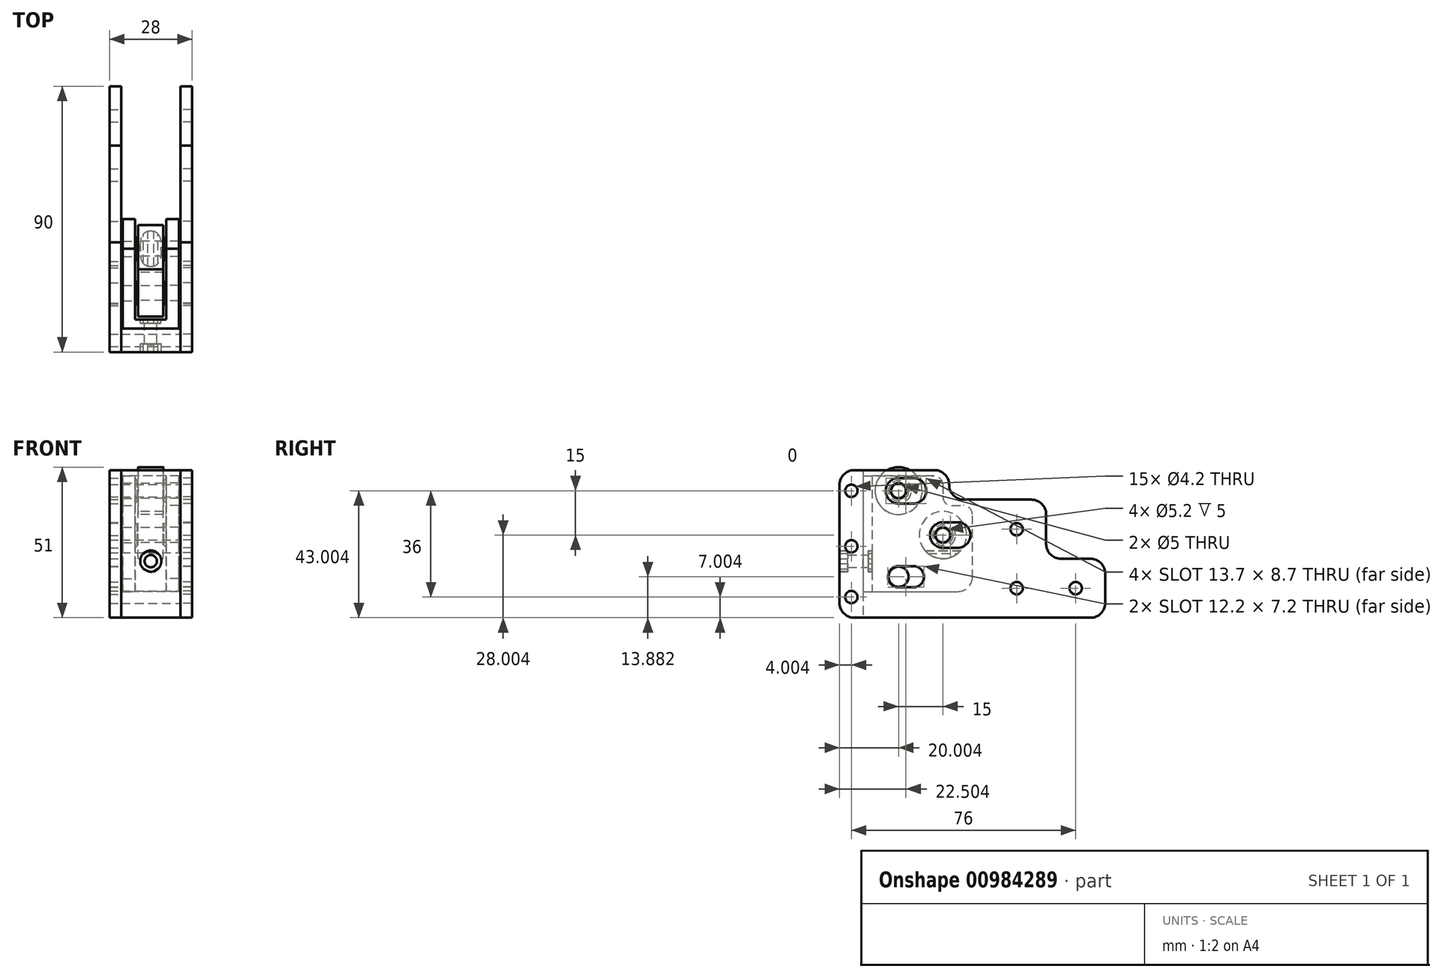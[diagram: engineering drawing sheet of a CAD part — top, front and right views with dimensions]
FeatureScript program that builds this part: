
annotation { "Feature Type Name" : "Feature", "Feature Type Description" : "" }
export const myFeature = defineFeature(function(context is Context, id is Id, definition is map)
    precondition{}
    {
        {
            var Q0;
            Q0=qCreatedBy(makeId("Right.planeOp"),FACE);
            var sketch = newSketch(context, id + "F0", { "sketchPlane" : qUnion([Q0])});
            skLineSegment(sketch, "E0.top", {"start": v(-51.77, -24.19) * mm, "end": v(28.23, -24.19) * mm});
            skLineSegment(sketch, "E0.left", {"start": v(-56.77, 20.81) * mm, "end": v(-56.77, -19.19) * mm});
            skCircle(sketch, "E1", {"center": v(23.23, -14.19) * mm, "radius": 2.1 * mm});
            skCircle(sketch, "E2", {"center": v(3.23, -14.19) * mm, "radius": 2.1 * mm});
            skCircle(sketch, "E3", {"center": v(3.23, 5.81) * mm, "radius": 2.1 * mm});
            skArc(sketch, "E4", {"start": v(-31.77, 14.46) * mm, "mid": v(-27.42, 18.81) * mm, "end": v(-31.77, 23.16) * mm});
            skLineSegment(sketch, "E5", {"start": v(-31.77, 23.16) * mm, "end": v(-36.77, 23.16) * mm});
            skLineSegment(sketch, "E6", {"start": v(-31.77, 14.46) * mm, "end": v(-36.77, 14.46) * mm});
            skArc(sketch, "E7", {"start": v(-36.77, 23.16) * mm, "mid": v(-41.12, 18.81) * mm, "end": v(-36.77, 14.46) * mm});
            skArc(sketch, "E8", {"start": v(-16.77, -0.54) * mm, "mid": v(-12.42, 3.81) * mm, "end": v(-16.77, 8.16) * mm});
            skLineSegment(sketch, "E9", {"start": v(-16.77, 8.16) * mm, "end": v(-21.77, 8.16) * mm});
            skLineSegment(sketch, "E10", {"start": v(-16.77, -0.54) * mm, "end": v(-21.77, -0.54) * mm});
            skArc(sketch, "E11", {"start": v(-21.77, 8.16) * mm, "mid": v(-26.12, 3.81) * mm, "end": v(-21.77, -0.54) * mm});
            skCircle(sketch, "E12", {"center": v(-52.77, 18.81) * mm, "radius": 2.1 * mm});
            skCircle(sketch, "E13", {"center": v(-52.77, -17.19) * mm, "radius": 2.1 * mm});
            skCircle(sketch, "E14", {"center": v(-52.77, 0) * mm, "radius": 2.1 * mm});
            skLineSegment(sketch, "E15", {"start": v(-19.64, 20.81) * mm, "end": v(-19.64, 20.81) * mm});
            skLineSegment(sketch, "E16", {"start": v(-14.64, 15.81) * mm, "end": v(8.23, 15.81) * mm});
            skLineSegment(sketch, "E17", {"start": v(13.23, 10.81) * mm, "end": v(13.23, 0.81) * mm});
            skLineSegment(sketch, "E18", {"start": v(18.23, -4.19) * mm, "end": v(28.23, -4.19) * mm});
            skLineSegment(sketch, "E19", {"start": v(-24.64, 25.81) * mm, "end": v(-51.77, 25.81) * mm});
            skLineSegment(sketch, "E20", {"start": v(33.23, -9.19) * mm, "end": v(33.23, -19.19) * mm});
            skPoint(sketch, "E21.visualSharp", {"position": v(-56.77, 25.81) * mm});
            skArc(sketch, "E21.filletArc", {"start": v(-51.77, 25.81) * mm, "mid": v(-55.3, 24.35) * mm, "end": v(-56.77, 20.81) * mm});
            skPoint(sketch, "E22.visualSharp", {"position": v(-56.77, -24.19) * mm});
            skArc(sketch, "E22.filletArc", {"start": v(-56.77, -19.19) * mm, "mid": v(-55.3, -22.72) * mm, "end": v(-51.77, -24.19) * mm});
            skPoint(sketch, "E23.visualSharp", {"position": v(-19.64, 25.81) * mm});
            skArc(sketch, "E23.filletArc", {"start": v(-19.64, 20.81) * mm, "mid": v(-21.1, 24.35) * mm, "end": v(-24.64, 25.81) * mm});
            skPoint(sketch, "E24.visualSharp", {"position": v(-19.64, 15.81) * mm});
            skArc(sketch, "E24.filletArc", {"start": v(-19.64, 20.81) * mm, "mid": v(-18.18, 17.28) * mm, "end": v(-14.64, 15.81) * mm});
            skPoint(sketch, "E25.visualSharp", {"position": v(13.23, 15.81) * mm});
            skArc(sketch, "E25.filletArc", {"start": v(13.23, 10.81) * mm, "mid": v(11.77, 14.35) * mm, "end": v(8.23, 15.81) * mm});
            skPoint(sketch, "E26.visualSharp", {"position": v(13.23, -4.19) * mm});
            skArc(sketch, "E26.filletArc", {"start": v(13.23, 0.81) * mm, "mid": v(14.7, -2.72) * mm, "end": v(18.23, -4.19) * mm});
            skPoint(sketch, "E27.visualSharp", {"position": v(33.23, -4.19) * mm});
            skArc(sketch, "E27.filletArc", {"start": v(33.23, -9.19) * mm, "mid": v(31.77, -5.65) * mm, "end": v(28.23, -4.19) * mm});
            skPoint(sketch, "E28.visualSharp", {"position": v(33.23, -24.19) * mm});
            skArc(sketch, "E28.filletArc", {"start": v(28.23, -24.19) * mm, "mid": v(31.77, -22.72) * mm, "end": v(33.23, -19.19) * mm});
            skLineSegment(sketch, "E29", {"start": v(-48.77, 25.81) * mm, "end": v(-48.77, -24.19) * mm});
            skArc(sketch, "E30", {"start": v(-36.77, -6.7) * mm, "mid": v(-40.37, -10.3) * mm, "end": v(-36.77, -13.9) * mm});
            skLineSegment(sketch, "E31", {"start": v(-36.77, -6.7) * mm, "end": v(-31.77, -6.7) * mm});
            skLineSegment(sketch, "E32", {"start": v(-36.77, -13.9) * mm, "end": v(-31.77, -13.9) * mm});
            skArc(sketch, "E33", {"start": v(-31.77, -13.9) * mm, "mid": v(-28.17, -10.3) * mm, "end": v(-31.77, -6.7) * mm});
            skSolve(sketch);
        }
        {
            var Q0;
            Q0 = qSketchRegion(id + "F0", true);
            extrude(context, id + "F1", {"entities" : qUnion([Q0]), "depth" : 14 * mm, "offsetDistance" : 25 * mm, "hasSecondDirection" : true, "secondDirectionOppositeDirection" : false, "secondDirectionDepth" : 10 * mm});
        }
        {
            var Q0;
            Q0 = qSketchRegion(id + "F0", true);
            extrude(context, id + "F2", {"entities" : qUnion([Q0]), "oppositeDirection" : true, "depth" : 14 * mm, "offsetDistance" : 25 * mm, "hasSecondDirection" : true, "secondDirectionOppositeDirection" : true, "secondDirectionDepth" : 10 * mm});
        }
        {
            var Q0;
            Q0=qCreatedBy(makeId("Right.planeOp"),FACE);
            var sketch = newSketch(context, id + "F3", { "sketchPlane" : qUnion([Q0])});
            skCircle(sketch, "E34", {"center": v(-36.77, 18.81) * mm, "radius": 8 * mm});
            skCircle(sketch, "E35", {"center": v(-21.77, 3.81) * mm, "radius": 8 * mm});
            skCircle(sketch, "E36", {"center": v(-36.77, 18.81) * mm, "radius": 2.5 * mm});
            skCircle(sketch, "E37", {"center": v(-21.77, 3.81) * mm, "radius": 2.5 * mm});
            skSolve(sketch);
        }
        {
            var Q0;
            Q0 = qSketchRegion(id + "F3", true);
            extrude(context, id + "F4", {"entities" : qUnion([Q0]), "depth" : 4.25 * mm, "offsetDistance" : 25 * mm, "hasSecondDirection" : true, "secondDirectionOppositeDirection" : true, "secondDirectionDepth" : 4.25 * mm});
        }
        {
            var Q0;
            Q0=makeQuery(id+"F0.imprint","IMPRINT",FACE,{"disambiguationData":[TD([[makeQuery(id+"F0.imprint","IMPRINT",EDGE,{"derivedFrom":sQuery(id+"F0.wireOp",EDGE,"E0.left")}),1.0]])]});
            extrude(context, id + "F5", {"entities" : qUnion([Q0]), "oppositeDirection" : true, "depth" : 10 * mm, "offsetDistance" : 25 * mm, "hasSecondDirection" : true, "secondDirectionOppositeDirection" : false, "secondDirectionDepth" : 10 * mm});
        }
        {
            var Q0;
            Q0=qCreatedBy(makeId("Right.planeOp"),FACE);
            var sketch = newSketch(context, id + "F6", { "sketchPlane" : qUnion([Q0])});
            skLineSegment(sketch, "E38.top", {"start": v(-48.77, -15.3) * mm, "end": v(-16.73, -15.3) * mm});
            skLineSegment(sketch, "E38.left", {"start": v(-48.77, 23.81) * mm, "end": v(-48.77, -15.3) * mm});
            skLineSegment(sketch, "E39", {"start": v(-45.77, 23.81) * mm, "end": v(-45.77, -15.3) * mm});
            skCircle(sketch, "E40", {"center": v(-21.77, 3.81) * mm, "radius": 2.6 * mm});
            skCircle(sketch, "E41", {"center": v(-36.77, 18.81) * mm, "radius": 2.6 * mm});
            skPoint(sketch, "E42.visualSharp", {"position": v(-11.77, -15.3) * mm});
            skArc(sketch, "E42.filletArc", {"start": v(-16.73, -15.3) * mm, "mid": v(-13.42, -14.06) * mm, "end": v(-11.77, -10.93) * mm});
            skCircle(sketch, "E43", {"center": v(-36.77, -10.3) * mm, "radius": 3.4 * mm});
            skLineSegment(sketch, "E44", {"start": v(-21.77, 20.81) * mm, "end": v(-21.77, 16.81) * mm});
            skLineSegment(sketch, "E45", {"start": v(-18.77, 13.81) * mm, "end": v(-14.77, 13.81) * mm});
            skLineSegment(sketch, "E46", {"start": v(-11.77, -10.93) * mm, "end": v(-11.77, 10.81) * mm});
            skLineSegment(sketch, "E47", {"start": v(-24.77, 23.81) * mm, "end": v(-45.77, 23.81) * mm});
            skLineSegment(sketch, "E48", {"start": v(-48.77, 23.81) * mm, "end": v(-45.77, 23.81) * mm});
            skPoint(sketch, "E49.visualSharp", {"position": v(-21.77, 23.81) * mm});
            skArc(sketch, "E49.filletArc", {"start": v(-21.77, 20.81) * mm, "mid": v(-22.65, 22.94) * mm, "end": v(-24.77, 23.81) * mm});
            skPoint(sketch, "E50.visualSharp", {"position": v(-21.77, 13.81) * mm});
            skArc(sketch, "E50.filletArc", {"start": v(-21.77, 16.81) * mm, "mid": v(-20.89, 14.7) * mm, "end": v(-18.77, 13.81) * mm});
            skPoint(sketch, "E51.visualSharp", {"position": v(-11.77, 13.81) * mm});
            skArc(sketch, "E51.filletArc", {"start": v(-11.77, 10.81) * mm, "mid": v(-12.65, 12.94) * mm, "end": v(-14.77, 13.81) * mm});
            skCircle(sketch, "E52", {"center": v(-36.77, 18.81) * mm, "radius": 4.25 * mm});
            skCircle(sketch, "E53", {"center": v(-21.77, 3.81) * mm, "radius": 4.25 * mm});
            skSolve(sketch);
        }
        {
            var Q0;
            {var subQ0=sQuery(id+"F6.wireOp",EDGE,"E38.left");Q0=makeQuery(id+"F6.imprint","IMPRINT",FACE,{"disambiguationData":[TD([[makeQuery(id+"F6.imprint","IMPRINT",EDGE,{"derivedFrom":subQ0}),1.0]])]});}
            extrude(context, id + "F7", {"entities" : qUnion([Q0]), "depth" : 9.5 * mm, "offsetDistance" : 25 * mm, "hasSecondDirection" : true, "secondDirectionOppositeDirection" : true, "secondDirectionDepth" : 9.5 * mm});
        }
        {
            var Q0;
            {var subQ0=sQuery(id+"F6.wireOp",EDGE,"E38.right");Q0=makeQuery(id+"F6.imprint","IMPRINT",FACE,{"disambiguationData":[TD([[makeQuery(id+"F6.imprint","IMPRINT",EDGE,{"derivedFrom":subQ0}),-1.0]])]});}
            var Q1;
            Q1=makeQuery(id+"F6.imprint","IMPRINT",FACE,{"disambiguationData":[TD([[makeQuery(id+"F6.imprint","IMPRINT",EDGE,{"derivedFrom":sQuery(id+"F6.wireOp",EDGE,"F1LG9TlT-1D1d-RnBV-PjZi-QMsiKcGYQHDK")}),1.0]])]});
            var Q2;
            Q2=makeQuery(id+"F6.imprint","IMPRINT",FACE,{"disambiguationData":[TD([[makeQuery(id+"F6.imprint","IMPRINT",EDGE,{"derivedFrom":sQuery(id+"F6.wireOp",EDGE,"E43")}),1.0]])]});
            var Q3;
            {var subQ2=sQuery(id+"F6.wireOp",EDGE,"E39");Q3=makeQuery(id+"F6.imprint","IMPRINT",FACE,{"disambiguationData":[TD([[makeQuery(id+"F6.imprint","IMPRINT",EDGE,{"derivedFrom":subQ2}),1.0]])]});}
            var Q4;
            Q4=makeQuery(id+"F6.imprint","IMPRINT",FACE,{"disambiguationData":[TD([[makeQuery(id+"F6.imprint","IMPRINT",EDGE,{"derivedFrom":sQuery(id+"F6.wireOp",EDGE,"E41")}),-1.0]])]});
            var Q5;
            Q5=makeQuery(id+"F6.imprint","IMPRINT",FACE,{"disambiguationData":[TD([[makeQuery(id+"F6.imprint","IMPRINT",EDGE,{"derivedFrom":sQuery(id+"F6.wireOp",EDGE,"E40")}),-1.0]])]});
            extrude(context, id + "F8", {"entities" : qUnion([Q0, Q1, Q2, Q3, Q4, Q5]), "operationType" : NewBodyOperationType.ADD, "depth" : 9.5 * mm, "offsetDistance" : 25 * mm, "hasSecondDirection" : true, "secondDirectionOppositeDirection" : false, "secondDirectionDepth" : 5.3 * mm});
        }
        {
            var Q0;
            {var subQ0=sQuery(id+"F6.wireOp",EDGE,"E38.right");Q0=makeQuery(id+"F6.imprint","IMPRINT",FACE,{"disambiguationData":[TD([[makeQuery(id+"F6.imprint","IMPRINT",EDGE,{"derivedFrom":subQ0}),-1.0]])]});}
            var Q1;
            Q1=makeQuery(id+"F6.imprint","IMPRINT",FACE,{"disambiguationData":[TD([[makeQuery(id+"F6.imprint","IMPRINT",EDGE,{"derivedFrom":sQuery(id+"F6.wireOp",EDGE,"F1LG9TlT-1D1d-RnBV-PjZi-QMsiKcGYQHDK")}),1.0]])]});
            var Q2;
            Q2=makeQuery(id+"F6.imprint","IMPRINT",FACE,{"disambiguationData":[TD([[makeQuery(id+"F6.imprint","IMPRINT",EDGE,{"derivedFrom":sQuery(id+"F6.wireOp",EDGE,"E43")}),1.0]])]});
            var Q3;
            {var subQ2=sQuery(id+"F6.wireOp",EDGE,"E39");Q3=makeQuery(id+"F6.imprint","IMPRINT",FACE,{"disambiguationData":[TD([[makeQuery(id+"F6.imprint","IMPRINT",EDGE,{"derivedFrom":subQ2}),1.0]])]});}
            var Q4;
            Q4=makeQuery(id+"F6.imprint","IMPRINT",FACE,{"disambiguationData":[TD([[makeQuery(id+"F6.imprint","IMPRINT",EDGE,{"derivedFrom":sQuery(id+"F6.wireOp",EDGE,"E41")}),-1.0]])]});
            var Q5;
            Q5=makeQuery(id+"F6.imprint","IMPRINT",FACE,{"disambiguationData":[TD([[makeQuery(id+"F6.imprint","IMPRINT",EDGE,{"derivedFrom":sQuery(id+"F6.wireOp",EDGE,"E40")}),-1.0]])]});
            extrude(context, id + "F9", {"entities" : qUnion([Q0, Q1, Q2, Q3, Q4, Q5]), "operationType" : NewBodyOperationType.ADD, "oppositeDirection" : true, "depth" : 9.5 * mm, "offsetDistance" : 25 * mm, "hasSecondDirection" : true, "secondDirectionOppositeDirection" : true, "secondDirectionDepth" : 5.3 * mm});
        }
        {
            var Q0;
            Q0=makeQuery(id+"F6.imprint","IMPRINT",FACE,{"disambiguationData":[TD([[makeQuery(id+"F6.imprint","IMPRINT",EDGE,{"derivedFrom":sQuery(id+"F6.wireOp",EDGE,"E43")}),1.0]])]});
            extrude(context, id + "F10", {"entities" : qUnion([Q0]), "operationType" : NewBodyOperationType.ADD, "depth" : 14 * mm, "offsetDistance" : 25 * mm, "hasSecondDirection" : true, "secondDirectionOppositeDirection" : false, "secondDirectionDepth" : 9.5 * mm});
        }
        {
            var Q0;
            Q0=makeQuery(id+"F6.imprint","IMPRINT",FACE,{"disambiguationData":[TD([[makeQuery(id+"F6.imprint","IMPRINT",EDGE,{"derivedFrom":sQuery(id+"F6.wireOp",EDGE,"E43")}),1.0]])]});
            extrude(context, id + "F11", {"entities" : qUnion([Q0]), "operationType" : NewBodyOperationType.ADD, "oppositeDirection" : true, "depth" : 14 * mm, "offsetDistance" : 25 * mm, "hasSecondDirection" : true, "secondDirectionOppositeDirection" : true, "secondDirectionDepth" : 9.5 * mm});
        }
        {
            var Q0;
            Q0=makeQuery(id+"F6.imprint","IMPRINT",FACE,{"disambiguationData":[TD([[makeQuery(id+"F6.imprint","IMPRINT",EDGE,{"derivedFrom":sQuery(id+"F6.wireOp",EDGE,"E41")}),-1.0]])]});
            var Q1;
            Q1=makeQuery(id+"F6.imprint","IMPRINT",FACE,{"disambiguationData":[TD([[makeQuery(id+"F6.imprint","IMPRINT",EDGE,{"derivedFrom":sQuery(id+"F6.wireOp",EDGE,"E40")}),-1.0]])]});
            extrude(context, id + "F12", {"entities" : qUnion([Q0, Q1]), "operationType" : NewBodyOperationType.ADD, "depth" : 5.3 * mm, "offsetDistance" : 25 * mm, "hasSecondDirection" : true, "secondDirectionOppositeDirection" : false, "secondDirectionDepth" : 4.5 * mm});
        }
        {
            var Q0;
            Q0=makeQuery(id+"F6.imprint","IMPRINT",FACE,{"disambiguationData":[TD([[makeQuery(id+"F6.imprint","IMPRINT",EDGE,{"derivedFrom":sQuery(id+"F6.wireOp",EDGE,"E41")}),-1.0]])]});
            var Q1;
            Q1=makeQuery(id+"F6.imprint","IMPRINT",FACE,{"disambiguationData":[TD([[makeQuery(id+"F6.imprint","IMPRINT",EDGE,{"derivedFrom":sQuery(id+"F6.wireOp",EDGE,"E40")}),-1.0]])]});
            extrude(context, id + "F13", {"entities" : qUnion([Q0, Q1]), "operationType" : NewBodyOperationType.ADD, "oppositeDirection" : true, "depth" : 5.3 * mm, "offsetDistance" : 25 * mm, "hasSecondDirection" : true, "secondDirectionOppositeDirection" : true, "secondDirectionDepth" : 4.5 * mm});
        }
        {
            var Q0;
            Q0=makeQuery(id+"F13.opExtrude","CAP_EDGE",EDGE,{"disambiguationData":[OSD([sQuery(id+"F6.wireOp",EDGE,"E52")])],"isStart":true});
            var Q1;
            Q1=makeQuery(id+"F13.opExtrude","CAP_EDGE",EDGE,{"disambiguationData":[OSD([sQuery(id+"F6.wireOp",EDGE,"E53")])],"isStart":true});
            var Q2;
            Q2=makeQuery(id+"F12.opExtrude","CAP_EDGE",EDGE,{"disambiguationData":[OSD([sQuery(id+"F6.wireOp",EDGE,"E53")])],"isStart":true});
            var Q3;
            Q3=makeQuery(id+"F12.opExtrude","CAP_EDGE",EDGE,{"disambiguationData":[OSD([sQuery(id+"F6.wireOp",EDGE,"E52")])],"isStart":true});
            chamfer(context, id + "F14", {"entities" : qUnion([Q0, Q1, Q2, Q3]), "width" : 0.8 * mm, "tangentPropagation" : true});
        }
        {
            var Q0;
            Q0=qCreatedBy(makeId("Front.planeOp"),FACE);
            var sketch = newSketch(context, id + "F15", { "sketchPlane" : qUnion([Q0])});
            skCircle(sketch, "E54", {"center": v(0, -5) * mm, "radius": 2.1 * mm});
            skCircle(sketch, "E55", {"center": v(0, -5) * mm, "radius": 3.6 * mm});
            skCircle(sketch, "E56.cCircle", {"center": v(0, -5) * mm, "radius": 3.5 * mm, "construction": true});
            skLineSegment(sketch, "E56.0", {"start": v(-3.49, -2.95) * mm, "end": v(0.03, -0.96) * mm});
            skLineSegment(sketch, "E56.1", {"start": v(0.03, -0.96) * mm, "end": v(3.51, -3) * mm});
            skLineSegment(sketch, "E56.2", {"start": v(3.51, -3) * mm, "end": v(3.49, -7.05) * mm});
            skLineSegment(sketch, "E56.3", {"start": v(3.49, -7.05) * mm, "end": v(-0.03, -9.04) * mm});
            skLineSegment(sketch, "E56.4", {"start": v(-0.03, -9.04) * mm, "end": v(-3.51, -7) * mm});
            skLineSegment(sketch, "E56.5", {"start": v(-3.51, -7) * mm, "end": v(-3.49, -2.95) * mm});
            skPoint(sketch, "E56.0.midPoint", {"position": v(-1.73, -1.96) * mm});
            skSolve(sketch);
        }
        {
            var Q0;
            Q0=makeQuery(id+"F15.imprint","IMPRINT",FACE,{"disambiguationData":[TD([[makeQuery(id+"F15.imprint","IMPRINT",EDGE,{"derivedFrom":sQuery(id+"F15.wireOp",EDGE,"E54")}),1.0]])]});
            extrude(context, id + "F16", {"entities" : qUnion([Q0]), "operationType" : NewBodyOperationType.REMOVE, "endBound" : BoundingType.THROUGH_ALL, "depth" : 25 * mm, "offsetDistance" : 25 * mm});
        }
        {
            var Q0;
            {var subQ0=sQuery(id+"F15.wireOp",EDGE,"E56.0");var subQ1=sQuery(id+"F15.wireOp",EDGE,"E55");var subQ2=makeQuery(id+"F15.imprint","INTERSECT",VERTEX,{"disambiguationData":[OD(1.0)],"derivedFrom":[subQ1,subQ0]});Q0=makeQuery(id+"F15.imprint","IMPRINT",FACE,{"disambiguationData":[TD([[makeQuery(id+"F15.imprint","IMPRINT",EDGE,{"disambiguationData":[TD([[subQ2,-1.0]])],"derivedFrom":subQ1}),-1.0]])]});}
            var Q1;
            {var subQ0=sQuery(id+"F15.wireOp",EDGE,"E56.1");var subQ1=sQuery(id+"F15.wireOp",EDGE,"E55");var subQ2=makeQuery(id+"F15.imprint","INTERSECT",VERTEX,{"disambiguationData":[OD(1.0)],"derivedFrom":[subQ1,subQ0]});Q1=makeQuery(id+"F15.imprint","IMPRINT",FACE,{"disambiguationData":[TD([[makeQuery(id+"F15.imprint","IMPRINT",EDGE,{"disambiguationData":[TD([[subQ2,-1.0]])],"derivedFrom":subQ1}),-1.0]])]});}
            var Q2;
            {var subQ0=sQuery(id+"F15.wireOp",EDGE,"E56.1");var subQ1=sQuery(id+"F15.wireOp",EDGE,"E55");var subQ2=makeQuery(id+"F15.imprint","INTERSECT",VERTEX,{"disambiguationData":[OD(0.0)],"derivedFrom":[subQ1,subQ0]});Q2=makeQuery(id+"F15.imprint","IMPRINT",FACE,{"disambiguationData":[TD([[makeQuery(id+"F15.imprint","IMPRINT",EDGE,{"disambiguationData":[TD([[subQ2,1.0]])],"derivedFrom":subQ1}),-1.0]])]});}
            var Q3;
            {var subQ0=sQuery(id+"F15.wireOp",EDGE,"E56.3");var subQ1=sQuery(id+"F15.wireOp",EDGE,"E55");var subQ2=makeQuery(id+"F15.imprint","INTERSECT",VERTEX,{"disambiguationData":[OD(1.0)],"derivedFrom":[subQ1,subQ0]});Q3=makeQuery(id+"F15.imprint","IMPRINT",FACE,{"disambiguationData":[TD([[makeQuery(id+"F15.imprint","IMPRINT",EDGE,{"disambiguationData":[TD([[subQ2,-1.0]])],"derivedFrom":subQ1}),-1.0]])]});}
            var Q4;
            {var subQ0=sQuery(id+"F15.wireOp",EDGE,"E56.5");var subQ1=sQuery(id+"F15.wireOp",EDGE,"E55");var subQ2=makeQuery(id+"F15.imprint","INTERSECT",VERTEX,{"disambiguationData":[OD(1.0)],"derivedFrom":[subQ1,subQ0]});Q4=makeQuery(id+"F15.imprint","IMPRINT",FACE,{"disambiguationData":[TD([[makeQuery(id+"F15.imprint","IMPRINT",EDGE,{"disambiguationData":[TD([[subQ2,-1.0]])],"derivedFrom":subQ1}),-1.0]])]});}
            var Q5;
            {var subQ0=sQuery(id+"F15.wireOp",EDGE,"E56.4");var subQ1=sQuery(id+"F15.wireOp",EDGE,"E55");var subQ2=makeQuery(id+"F15.imprint","INTERSECT",VERTEX,{"disambiguationData":[OD(1.0)],"derivedFrom":[subQ1,subQ0]});Q5=makeQuery(id+"F15.imprint","IMPRINT",FACE,{"disambiguationData":[TD([[makeQuery(id+"F15.imprint","IMPRINT",EDGE,{"disambiguationData":[TD([[subQ2,-1.0]])],"derivedFrom":subQ1}),-1.0]])]});}
            var Q6;
            Q6=makeQuery(id+"F15.imprint","IMPRINT",FACE,{"disambiguationData":[TD([[makeQuery(id+"F15.imprint","IMPRINT",EDGE,{"derivedFrom":sQuery(id+"F15.wireOp",EDGE,"E54")}),-1.0]])]});
            var Q7;
            Q7=makeQuery(id+"F15.imprint","IMPRINT",FACE,{"disambiguationData":[TD([[makeQuery(id+"F15.imprint","IMPRINT",EDGE,{"derivedFrom":sQuery(id+"F15.wireOp",EDGE,"E54")}),1.0]])]});
            extrude(context, id + "F17", {"entities" : qUnion([Q0, Q1, Q2, Q3, Q4, Q5, Q6, Q7]), "operationType" : NewBodyOperationType.REMOVE, "depth" : 47 * mm, "offsetDistance" : 25 * mm});
        }
        {
            var Q0;
            Q0=makeQuery(id+"F15.imprint","IMPRINT",FACE,{"disambiguationData":[TD([[makeQuery(id+"F15.imprint","IMPRINT",EDGE,{"derivedFrom":sQuery(id+"F15.wireOp",EDGE,"E54")}),-1.0]])]});
            var Q1;
            {var subQ0=sQuery(id+"F15.wireOp",EDGE,"E56.5");var subQ1=sQuery(id+"F15.wireOp",EDGE,"E55");var subQ2=makeQuery(id+"F15.imprint","INTERSECT",VERTEX,{"disambiguationData":[OD(0.0)],"derivedFrom":[subQ1,subQ0]});Q1=makeQuery(id+"F15.imprint","IMPRINT",FACE,{"disambiguationData":[TD([[makeQuery(id+"F15.imprint","IMPRINT",EDGE,{"disambiguationData":[TD([[subQ2,-1.0]])],"derivedFrom":subQ1}),1.0]])]});}
            var Q2;
            {var subQ0=sQuery(id+"F15.wireOp",EDGE,"E56.0");var subQ1=sQuery(id+"F15.wireOp",EDGE,"E55");var subQ2=makeQuery(id+"F15.imprint","INTERSECT",VERTEX,{"disambiguationData":[OD(0.0)],"derivedFrom":[subQ1,subQ0]});Q2=makeQuery(id+"F15.imprint","IMPRINT",FACE,{"disambiguationData":[TD([[makeQuery(id+"F15.imprint","IMPRINT",EDGE,{"disambiguationData":[TD([[subQ2,-1.0]])],"derivedFrom":subQ1}),1.0]])]});}
            var Q3;
            {var subQ0=sQuery(id+"F15.wireOp",EDGE,"E56.1");var subQ1=sQuery(id+"F15.wireOp",EDGE,"E55");var subQ2=makeQuery(id+"F15.imprint","INTERSECT",VERTEX,{"disambiguationData":[OD(0.0)],"derivedFrom":[subQ1,subQ0]});Q3=makeQuery(id+"F15.imprint","IMPRINT",FACE,{"disambiguationData":[TD([[makeQuery(id+"F15.imprint","IMPRINT",EDGE,{"disambiguationData":[TD([[subQ2,-1.0]])],"derivedFrom":subQ1}),1.0]])]});}
            var Q4;
            {var subQ0=sQuery(id+"F15.wireOp",EDGE,"E56.2");var subQ1=sQuery(id+"F15.wireOp",EDGE,"E55");var subQ2=makeQuery(id+"F15.imprint","INTERSECT",VERTEX,{"disambiguationData":[OD(0.0)],"derivedFrom":[subQ1,subQ0]});Q4=makeQuery(id+"F15.imprint","IMPRINT",FACE,{"disambiguationData":[TD([[makeQuery(id+"F15.imprint","IMPRINT",EDGE,{"disambiguationData":[TD([[subQ2,1.0]])],"derivedFrom":subQ1}),1.0]])]});}
            var Q5;
            {var subQ0=sQuery(id+"F15.wireOp",EDGE,"E56.3");var subQ1=sQuery(id+"F15.wireOp",EDGE,"E55");var subQ2=makeQuery(id+"F15.imprint","INTERSECT",VERTEX,{"disambiguationData":[OD(0.0)],"derivedFrom":[subQ1,subQ0]});Q5=makeQuery(id+"F15.imprint","IMPRINT",FACE,{"disambiguationData":[TD([[makeQuery(id+"F15.imprint","IMPRINT",EDGE,{"disambiguationData":[TD([[subQ2,-1.0]])],"derivedFrom":subQ1}),1.0]])]});}
            var Q6;
            {var subQ0=sQuery(id+"F15.wireOp",EDGE,"E56.4");var subQ1=sQuery(id+"F15.wireOp",EDGE,"E55");var subQ2=makeQuery(id+"F15.imprint","INTERSECT",VERTEX,{"disambiguationData":[OD(0.0)],"derivedFrom":[subQ1,subQ0]});Q6=makeQuery(id+"F15.imprint","IMPRINT",FACE,{"disambiguationData":[TD([[makeQuery(id+"F15.imprint","IMPRINT",EDGE,{"disambiguationData":[TD([[subQ2,-1.0]])],"derivedFrom":subQ1}),1.0]])]});}
            extrude(context, id + "F18", {"entities" : qUnion([Q0, Q1, Q2, Q3, Q4, Q5, Q6]), "operationType" : NewBodyOperationType.REMOVE, "endBound" : BoundingType.THROUGH_ALL, "depth" : 25 * mm, "offsetDistance" : 25 * mm, "hasSecondDirection" : true, "secondDirectionOppositeDirection" : false, "secondDirectionDepth" : 54 * mm});
        }
    });
